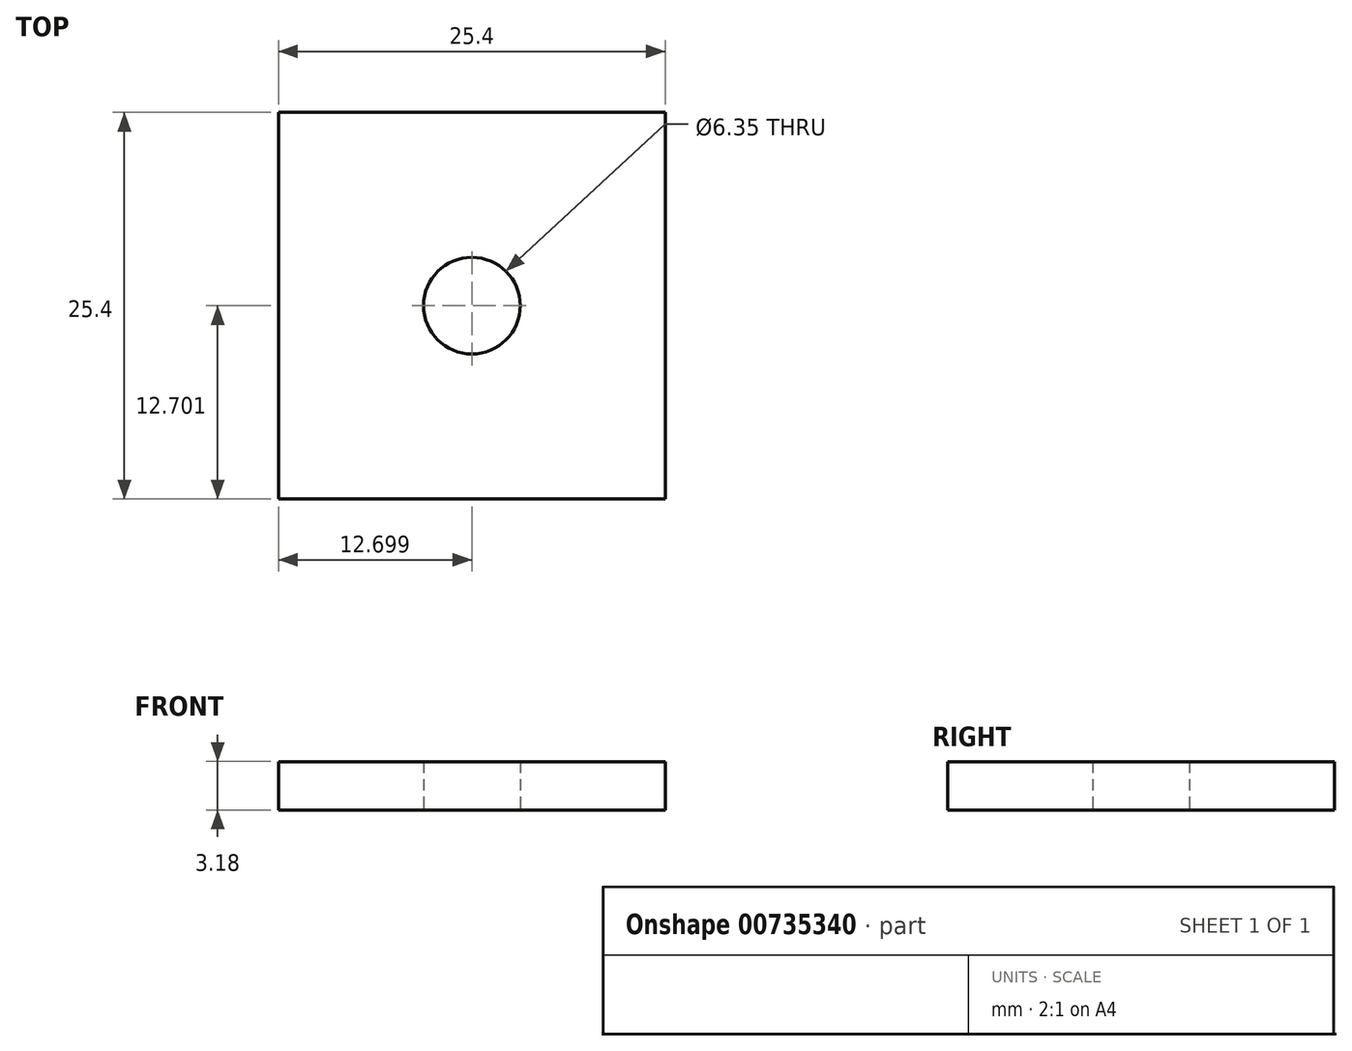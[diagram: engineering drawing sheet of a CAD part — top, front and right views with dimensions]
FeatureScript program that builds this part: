
annotation { "Feature Type Name" : "Feature", "Feature Type Description" : "" }
export const myFeature = defineFeature(function(context is Context, id is Id, definition is map)
    precondition{}
    {
        {
            var Q0;
            Q0=qCreatedBy(makeId("Top.planeOp"),FACE);
            var sketch = newSketch(context, id + "F0", { "sketchPlane" : qUnion([Q0])});
            skLineSegment(sketch, "E0.bottom", {"start": v(-55.87, 40.38) * mm, "end": v(-30.47, 40.38) * mm});
            skLineSegment(sketch, "E0.top", {"start": v(-55.87, 14.98) * mm, "end": v(-30.47, 14.98) * mm});
            skLineSegment(sketch, "E0.left", {"start": v(-55.87, 40.38) * mm, "end": v(-55.87, 14.98) * mm});
            skLineSegment(sketch, "E0.right", {"start": v(-30.47, 40.38) * mm, "end": v(-30.47, 14.98) * mm});
            skCircle(sketch, "E1", {"center": v(-43.17, 27.68) * mm, "radius": 3.18 * mm});
            skPoint(sketch, "E1.centerSnap0", {"position": v(-30.47, 27.68) * mm});
            skPoint(sketch, "E1.centerSnap1", {"position": v(-43.17, 14.98) * mm});
            skSolve(sketch);
        }
        {
            var Q0;
            Q0=makeQuery(id+"F0.imprint","IMPRINT",FACE,{"disambiguationData":[TD([[makeQuery(id+"F0.imprint","IMPRINT",EDGE,{"derivedFrom":sQuery(id+"F0.wireOp",EDGE,"E0.bottom")}),-1.0]])]});
            extrude(context, id + "F1", {"entities" : qUnion([Q0]), "depth" : 3.17 * mm, "offsetDistance" : 25.4 * mm});
        }
    });
